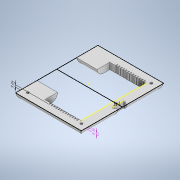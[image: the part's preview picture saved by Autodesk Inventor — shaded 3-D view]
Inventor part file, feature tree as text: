
AUTODESK INVENTOR PART (.ipt)
format: ipt  version: 2020 (Build 240168000, 168)  size: 1,347,584 bytes
history: native  units: mm
features: other x9, sketch x6, fillet x5, extrude x4, chamfer x1
ambient origin geometry x8: Origin, YZ Plane, XZ Plane, XY Plane, X Axis, Y Axis, Z Axis, Center Point
bodies: Body1 (feature_tree), Body2 (feature_tree), Body3 (feature_tree)
feature tree (25):
  other  "Casing_LCD_lip.ipt"
  other  "Annotations"
  extrude  "Extrusion5"  Depth=10.0mm
  chamfer  "Chamfer2"  Distance=3.0mm
  fillet  "Fillet7"  Radius=3.0mm
  fillet  "Fillet8"  Radius=3.0mm
  fillet  "Fillet9"  Radius=3.0mm
  fillet  "Fillet10"  Radius=3.0mm
  fillet  "Fillet11"  Radius=3.0mm
  extrude  "Extrusion7"  Depth=3.0mm
  sketch  "Sketch6"  dims[d24=3.0mm]
  extrude  "Extrusion8"  Depth=3.0mm
  extrude  "Extrusion9"  Depth=3.0mm
  other  "TaggingFeature1"
  sketch  "Sketch1"  dims[d0=10.0mm d19=55.0mm]
  other  "Srf2"
  sketch  "Sketch2"  dims[d20=55.0mm]
  sketch  "Sketch5"  dims[d23=9.7mm]
  sketch  "Sketch7"  dims[d25=3.0mm]
  sketch  "Sketch11"  dims[d26=3.0mm d27=3.0mm d28=3.0mm d29=3.0mm d30=3.0mm d31=3.0mm d32=3.0mm d33=3.0mm d34=7.05mm d35=7.05mm d36=7.05mm d37=7.05mm d38=7.05mm d39=7.05mm d40=7.05mm d41=7.05mm d42=7.05mm d43=3.0mm d44=3.0mm d45=3.0mm d46=7.05mm d47=7.05mm d48=7.05mm d49=354.6mm d50=177.3mm d52=10.0mm d53=0.0mm d57=30.0mm d75=17.0mm d76=2.0mm d77=45.0deg d82=28.0mm d83=4.0mm d84=1.0mm d85=4.0mm d89=2.0mm d90=10.0mm d93=10.0mm d94=50.0mm d95=40.0mm d96=20.0mm d97=25.0mm d99=27.4mm d100=0.0mm d101=10.0mm d102=282.0mm d103=141.0mm d123=10.0mm d124=5.0mm d125=0.0mm d126=0.0mm d129=10.0mm d130=16.0mm d131=16.0mm d132=16.0mm d133=16.0mm d134=3.0mm d135=0.0mm d136=1.0mm d137=1.0mm d78=1.696472mm d79=1.810348mm d80=9.1mm d86=5.107216mm d87=5.621346mm d88=9.043146mm d54=0.5mm d55=0.872665mm]
  other  "Solid1::Casing_LCD_lip.ipt"
  other  "Srf1"
  other  "Srf1::Derived"
  other  "Linear Dimension 1"
  other  "Linear Dimension 2"
